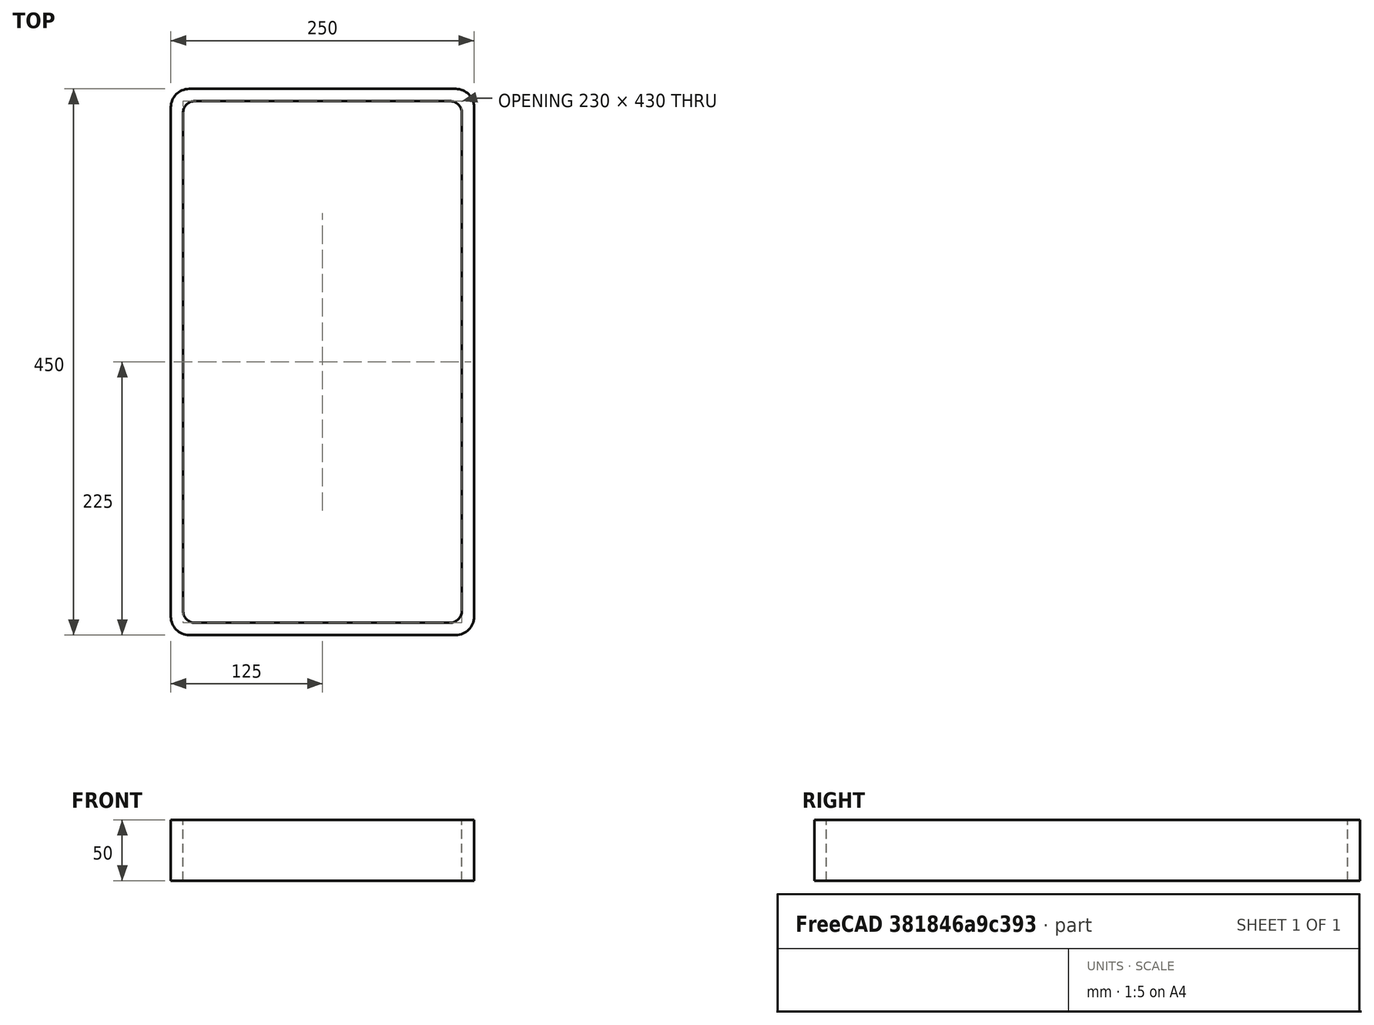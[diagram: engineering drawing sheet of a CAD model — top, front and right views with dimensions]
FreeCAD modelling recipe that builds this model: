
FCSTD DOCUMENT  (FreeCAD 0.15R4671 (Git))
Label: Rectangular hollow section 450x250x10 EN10219 S235JRH
License: All rights reserved
LicenseURL: http://en.wikipedia.org/wiki/All_rights_reserved
objects: Sketcher::SketchObject×1, Part::Extrusion×1
note: 2 computed .brp shape members not serialized (recipe doc carries the construction recipe); baked Part::Feature solids carry a one-line shape summary decoded from their .brp

FEATURE [Sketcher::SketchObject] Sketch
  sketch-geometry (16):
    g0: LineSegment StartX=-105 StartY=215 StartZ=0 EndX=105 EndY=215 EndZ=0
    g1: LineSegment StartX=115 StartY=205 StartZ=0 EndX=115 EndY=-205 EndZ=0
    g2: LineSegment StartX=105 StartY=-215 StartZ=0 EndX=-105 EndY=-215 EndZ=0
    g3: LineSegment StartX=-115 StartY=-205 StartZ=0 EndX=-115 EndY=205 EndZ=0
    g4: LineSegment StartX=-110 StartY=225 StartZ=0 EndX=110 EndY=225 EndZ=0
    g5: LineSegment StartX=125 StartY=210 StartZ=0 EndX=125 EndY=-210 EndZ=0
    g6: LineSegment StartX=110 StartY=-225 StartZ=0 EndX=-110 EndY=-225 EndZ=0
    g7: LineSegment StartX=-125 StartY=-210 StartZ=0 EndX=-125 EndY=210 EndZ=0
    g8: ArcOfCircle CenterX=-105 CenterY=205 CenterZ=0 NormalX=0 NormalY=0 NormalZ=1 Radius=10 StartAngle=1.5708 EndAngle=3.14159
    g9: ArcOfCircle CenterX=105 CenterY=205 CenterZ=0 NormalX=0 NormalY=0 NormalZ=1 Radius=10 StartAngle=0 EndAngle=1.5708
    g10: ArcOfCircle CenterX=105 CenterY=-205 CenterZ=0 NormalX=0 NormalY=0 NormalZ=1 Radius=10 StartAngle=4.71239 EndAngle=6.28319
    g11: ArcOfCircle CenterX=-105 CenterY=-205 CenterZ=0 NormalX=0 NormalY=0 NormalZ=1 Radius=10 StartAngle=3.14159 EndAngle=4.71239
    g12: ArcOfCircle CenterX=110 CenterY=210 CenterZ=0 NormalX=0 NormalY=0 NormalZ=1 Radius=15 StartAngle=0 EndAngle=1.5708
    g13: ArcOfCircle CenterX=110 CenterY=-210 CenterZ=0 NormalX=0 NormalY=0 NormalZ=1 Radius=15 StartAngle=4.71239 EndAngle=6.28319
    g14: ArcOfCircle CenterX=-110 CenterY=-210 CenterZ=0 NormalX=0 NormalY=0 NormalZ=1 Radius=15 StartAngle=3.14159 EndAngle=4.71239
    g15: ArcOfCircle CenterX=-110 CenterY=210 CenterZ=0 NormalX=0 NormalY=0 NormalZ=1 Radius=15 StartAngle=1.5708 EndAngle=3.14159
  constraints (36):
    c: Horizontal(g2)
    c: Vertical(g3)
    c: Horizontal(g6)
    c: Vertical(g7)
    c: Tangent(g3,g8) = 1.5708
    c: Tangent(g0,g8) = 1.5708
    c: Tangent(g0,g9) = 1.5708
    c: Tangent(g1,g9) = 1.5708
    c: Tangent(g1,g10) = 1.5708
    c: Tangent(g2,g10) = 1.5708
    c: Tangent(g2,g11) = 1.5708
    c: Tangent(g3,g11) = 1.5708
    c: Tangent(g4,g12) = 1.5708
    c: Tangent(g5,g12) = 1.5708
    c: Tangent(g5,g13) = 1.5708
    c: Tangent(g6,g13) = 1.5708
    c: Tangent(g6,g14) = 1.5708
    c: Tangent(g7,g14) = 1.5708
    c: Tangent(g7,g15) = 1.5708
    c: Tangent(g4,g15) = 1.5708
    c: Equal(g9,g8)
    c: Equal(g9,g11)
    c: Equal(g9,g10)
    c: Equal(g12,g15)
    c: Equal(g12,g14)
    c: Equal(g12,g13)
    c: Symmetric(g4,g6,g-1)
    c: Symmetric(g7,g5,g-2)
    c: DistanceY(g4,g6) = -450
    c: DistanceX(g7,g5) = 250
    c: Symmetric(g3,g1,g-2)
    c: Symmetric(g0,g2,g-1)
    c: DistanceY(g0,g4) = 10
    c: DistanceX(g5,g1) = -10
    c: Radius(g9) = 10
    c: Radius(g12) = 15
FEATURE [Part::Extrusion] Extrude  label="Rectangular hollow section 450x250x10 EN10219 S235JRH"
  Base = -> Sketch
  Dir = (0,0,50)
  Solid = true
